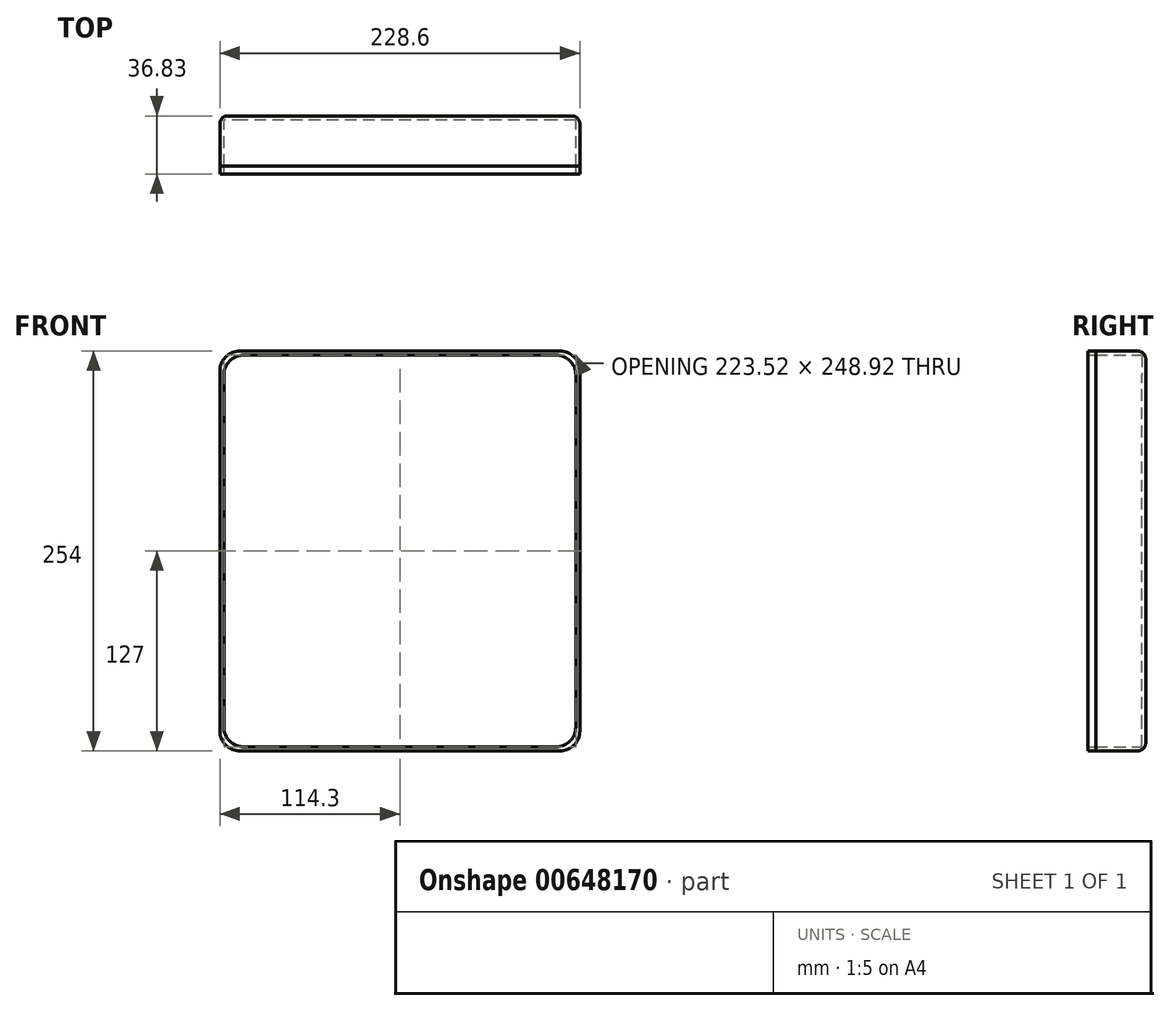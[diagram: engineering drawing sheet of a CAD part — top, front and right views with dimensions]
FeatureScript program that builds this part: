
annotation { "Feature Type Name" : "Feature", "Feature Type Description" : "" }
export const myFeature = defineFeature(function(context is Context, id is Id, definition is map)
    precondition{}
    {
        {
            var Q0;
            Q0=qCreatedBy(makeId("Front.planeOp"),FACE);
            var sketch = newSketch(context, id + "F0", { "sketchPlane" : qUnion([Q0])});
            skLineSegment(sketch, "E0.bottom", {"start": v(101.6, -127) * mm, "end": v(-101.6, -127) * mm});
            skLineSegment(sketch, "E0.top", {"start": v(101.6, 127) * mm, "end": v(-101.6, 127) * mm});
            skLineSegment(sketch, "E0.left", {"start": v(114.3, -114.3) * mm, "end": v(114.3, 114.3) * mm});
            skLineSegment(sketch, "E0.right", {"start": v(-114.3, -114.3) * mm, "end": v(-114.3, 114.3) * mm});
            skPoint(sketch, "E0.middle", {"position": v(0, 0) * mm});
            skPoint(sketch, "E1.visualSharp", {"position": v(-114.3, 127) * mm});
            skArc(sketch, "E1.filletArc", {"start": v(-101.6, 127) * mm, "mid": v(-110.58, 123.28) * mm, "end": v(-114.3, 114.3) * mm});
            skPoint(sketch, "E2.visualSharp", {"position": v(114.3, 127) * mm});
            skArc(sketch, "E2.filletArc", {"start": v(114.3, 114.3) * mm, "mid": v(110.58, 123.28) * mm, "end": v(101.6, 127) * mm});
            skPoint(sketch, "E3.visualSharp", {"position": v(114.3, -127) * mm});
            skArc(sketch, "E3.filletArc", {"start": v(101.6, -127) * mm, "mid": v(110.58, -123.28) * mm, "end": v(114.3, -114.3) * mm});
            skPoint(sketch, "E4.visualSharp", {"position": v(-114.3, -127) * mm});
            skArc(sketch, "E4.filletArc", {"start": v(-114.3, -114.3) * mm, "mid": v(-110.58, -123.28) * mm, "end": v(-101.6, -127) * mm});
            skPoint(sketch, "E5.visualSharp", {"position": v(-110.58, 123.28) * mm});
            skPoint(sketch, "E6.visualSharp", {"position": v(110.58, -123.28) * mm});
            skPoint(sketch, "E7.visualSharp", {"position": v(-110.58, -123.28) * mm});
            skLineSegment(sketch, "E8.bottom", {"start": v(99.06, -124.46) * mm, "end": v(-99.06, -124.46) * mm});
            skLineSegment(sketch, "E8.top", {"start": v(99.06, 124.46) * mm, "end": v(-99.06, 124.46) * mm});
            skLineSegment(sketch, "E8.left", {"start": v(111.76, -111.76) * mm, "end": v(111.76, 111.76) * mm});
            skLineSegment(sketch, "E8.right", {"start": v(-111.76, -111.76) * mm, "end": v(-111.76, 111.76) * mm});
            skPoint(sketch, "E9.visualSharp", {"position": v(111.76, 124.46) * mm});
            skArc(sketch, "E9.filletArc", {"start": v(111.76, 111.76) * mm, "mid": v(108.04, 120.74) * mm, "end": v(99.06, 124.46) * mm});
            skPoint(sketch, "E10.visualSharp", {"position": v(-111.76, 124.46) * mm});
            skArc(sketch, "E10.filletArc", {"start": v(-99.06, 124.46) * mm, "mid": v(-108.04, 120.74) * mm, "end": v(-111.76, 111.76) * mm});
            skPoint(sketch, "E11.visualSharp", {"position": v(-111.76, -124.46) * mm});
            skArc(sketch, "E11.filletArc", {"start": v(-111.76, -111.76) * mm, "mid": v(-108.04, -120.74) * mm, "end": v(-99.06, -124.46) * mm});
            skPoint(sketch, "E12.visualSharp", {"position": v(111.76, -124.46) * mm});
            skArc(sketch, "E12.filletArc", {"start": v(99.06, -124.46) * mm, "mid": v(108.04, -120.74) * mm, "end": v(111.76, -111.76) * mm});
            skSolve(sketch);
        }
        {
            var Q0;
            Q0=qSketchRegion(id+"F0",true);
            extrude(context, id + "F1", {"entities" : qUnion([Q0]), "depth" : 31.75 * mm, "offsetDistance" : 25.4 * mm});
        }
        {
            var Q0;
            Q0=qCreatedBy(makeId("Front.planeOp"),FACE);
            var sketch = newSketch(context, id + "F2", { "sketchPlane" : qUnion([Q0])});
            skLineSegment(sketch, "E13.bottom", {"start": v(-101.6, -127) * mm, "end": v(101.6, -127) * mm});
            skLineSegment(sketch, "E13.top", {"start": v(-101.6, 127) * mm, "end": v(101.6, 127) * mm});
            skLineSegment(sketch, "E13.left", {"start": v(-114.3, -114.3) * mm, "end": v(-114.3, 114.3) * mm});
            skLineSegment(sketch, "E13.right", {"start": v(114.3, -114.3) * mm, "end": v(114.3, 114.3) * mm});
            skPoint(sketch, "E13.middle", {"position": v(0, 0) * mm});
            skPoint(sketch, "E14.visualSharp", {"position": v(-114.3, 127) * mm});
            skArc(sketch, "E14.filletArc", {"start": v(-101.6, 127) * mm, "mid": v(-110.58, 123.28) * mm, "end": v(-114.3, 114.3) * mm});
            skPoint(sketch, "E15.visualSharp", {"position": v(114.3, 127) * mm});
            skArc(sketch, "E15.filletArc", {"start": v(114.3, 114.3) * mm, "mid": v(110.58, 123.28) * mm, "end": v(101.6, 127) * mm});
            skPoint(sketch, "E16.visualSharp", {"position": v(114.3, -127) * mm});
            skArc(sketch, "E16.filletArc", {"start": v(101.6, -127) * mm, "mid": v(110.58, -123.28) * mm, "end": v(114.3, -114.3) * mm});
            skPoint(sketch, "E17.visualSharp", {"position": v(-114.3, -127) * mm});
            skArc(sketch, "E17.filletArc", {"start": v(-114.3, -114.3) * mm, "mid": v(-110.58, -123.28) * mm, "end": v(-101.6, -127) * mm});
            skSolve(sketch);
        }
        {
            var Q0;
            Q0=qSketchRegion(id+"F2",true);
            extrude(context, id + "F3", {"entities" : qUnion([Q0]), "operationType" : NewBodyOperationType.ADD, "depth" : 2.54 * mm, "offsetDistance" : 25.4 * mm});
        }
        {
            var Q0;
            Q0=makeQuery(id+"F1.opExtrude","CAP_FACE",FACE,{"disambiguationData":[OSD([sQuery(id+"F0.wireOp",EDGE,"E0.bottom"),sQuery(id+"F0.wireOp",EDGE,"E0.top"),sQuery(id+"F0.wireOp",EDGE,"E0.left"),sQuery(id+"F0.wireOp",EDGE,"E0.right"),sQuery(id+"F0.wireOp",EDGE,"E1.filletArc"),sQuery(id+"F0.wireOp",EDGE,"E2.filletArc"),sQuery(id+"F0.wireOp",EDGE,"E3.filletArc"),sQuery(id+"F0.wireOp",EDGE,"E4.filletArc"),sQuery(id+"F0.wireOp",EDGE,"s5b6SUju-C0is-XQkz-XXGF-fU9U0Y8NX6aP.bottom"),sQuery(id+"F0.wireOp",EDGE,"s5b6SUju-C0is-XQkz-XXGF-fU9U0Y8NX6aP.top"),sQuery(id+"F0.wireOp",EDGE,"s5b6SUju-C0is-XQkz-XXGF-fU9U0Y8NX6aP.left"),sQuery(id+"F0.wireOp",EDGE,"s5b6SUju-C0is-XQkz-XXGF-fU9U0Y8NX6aP.right"),sQuery(id+"F0.wireOp",EDGE,"E5.filletArc"),sQuery(id+"F0.wireOp",EDGE,"b02a0fa0-6dca-4f1c-a319-37c0052a69da.filletArc"),sQuery(id+"F0.wireOp",EDGE,"E6.filletArc"),sQuery(id+"F0.wireOp",EDGE,"E7.filletArc")])],"isStart":false});
            var sketch = newSketch(context, id + "F4", { "sketchPlane" : qUnion([Q0])});
            skLineSegment(sketch, "E18.bottom", {"start": v(101.6, -127) * mm, "end": v(-101.6, -127) * mm});
            skLineSegment(sketch, "E18.top", {"start": v(101.6, 127) * mm, "end": v(-101.6, 127) * mm});
            skLineSegment(sketch, "E18.left", {"start": v(114.3, -114.3) * mm, "end": v(114.3, 114.3) * mm});
            skLineSegment(sketch, "E18.right", {"start": v(-114.3, -114.3) * mm, "end": v(-114.3, 114.3) * mm});
            skPoint(sketch, "E18.middle", {"position": v(0, 0) * mm});
            skPoint(sketch, "E19.visualSharp", {"position": v(-114.3, 127) * mm});
            skArc(sketch, "E19.filletArc", {"start": v(-101.6, 127) * mm, "mid": v(-110.58, 123.28) * mm, "end": v(-114.3, 114.3) * mm});
            skPoint(sketch, "E20.visualSharp", {"position": v(114.3, 127) * mm});
            skArc(sketch, "E20.filletArc", {"start": v(114.3, 114.3) * mm, "mid": v(110.58, 123.28) * mm, "end": v(101.6, 127) * mm});
            skPoint(sketch, "E21.visualSharp", {"position": v(114.3, -127) * mm});
            skArc(sketch, "E21.filletArc", {"start": v(101.6, -127) * mm, "mid": v(110.58, -123.28) * mm, "end": v(114.3, -114.3) * mm});
            skPoint(sketch, "E22.visualSharp", {"position": v(-114.3, -127) * mm});
            skArc(sketch, "E22.filletArc", {"start": v(-114.3, -114.3) * mm, "mid": v(-110.58, -123.28) * mm, "end": v(-101.6, -127) * mm});
            skPoint(sketch, "E23.visualSharp", {"position": v(-110.58, 123.28) * mm});
            skPoint(sketch, "E24.visualSharp", {"position": v(110.58, -123.28) * mm});
            skPoint(sketch, "E25.visualSharp", {"position": v(-106.9, -119.17) * mm});
            skLineSegment(sketch, "E26.bottom", {"start": v(99.06, -124.46) * mm, "end": v(-99.06, -124.46) * mm});
            skLineSegment(sketch, "E26.top", {"start": v(99.06, 124.46) * mm, "end": v(-99.06, 124.46) * mm});
            skLineSegment(sketch, "E26.left", {"start": v(111.76, -111.76) * mm, "end": v(111.76, 111.76) * mm});
            skLineSegment(sketch, "E26.right", {"start": v(-111.76, -111.76) * mm, "end": v(-111.76, 111.76) * mm});
            skPoint(sketch, "E27.visualSharp", {"position": v(111.76, 124.46) * mm});
            skArc(sketch, "E27.filletArc", {"start": v(111.76, 111.76) * mm, "mid": v(108.04, 120.74) * mm, "end": v(99.06, 124.46) * mm});
            skPoint(sketch, "E28.visualSharp", {"position": v(-111.76, 124.46) * mm});
            skArc(sketch, "E28.filletArc", {"start": v(-99.06, 124.46) * mm, "mid": v(-108.04, 120.74) * mm, "end": v(-111.76, 111.76) * mm});
            skPoint(sketch, "E29.visualSharp", {"position": v(-111.76, -124.46) * mm});
            skArc(sketch, "E29.filletArc", {"start": v(-111.76, -111.76) * mm, "mid": v(-108.04, -120.74) * mm, "end": v(-99.06, -124.46) * mm});
            skPoint(sketch, "E30.visualSharp", {"position": v(111.76, -124.46) * mm});
            skArc(sketch, "E30.filletArc", {"start": v(99.06, -124.46) * mm, "mid": v(108.04, -120.74) * mm, "end": v(111.76, -111.76) * mm});
            skSolve(sketch);
        }
        {
            var Q0;
            Q0=qSketchRegion(id+"F4",true);
            extrude(context, id + "F5", {"entities" : qUnion([Q0]), "depth" : 5.08 * mm, "offsetDistance" : 25.4 * mm});
        }
        {
            var Q0;
            Q0=makeQuery(id+"F3.boolean.opBoolean","MERGE",FACE,{"derivedFrom":[makeQuery(id+"F1.opExtrude","CAP_FACE",FACE,{"disambiguationData":[OSD([sQuery(id+"F0.wireOp",EDGE,"E0.bottom"),sQuery(id+"F0.wireOp",EDGE,"E0.top"),sQuery(id+"F0.wireOp",EDGE,"E0.left"),sQuery(id+"F0.wireOp",EDGE,"E0.right"),sQuery(id+"F0.wireOp",EDGE,"E1.filletArc"),sQuery(id+"F0.wireOp",EDGE,"E2.filletArc"),sQuery(id+"F0.wireOp",EDGE,"E3.filletArc"),sQuery(id+"F0.wireOp",EDGE,"E4.filletArc"),sQuery(id+"F0.wireOp",EDGE,"E8.bottom"),sQuery(id+"F0.wireOp",EDGE,"E8.top"),sQuery(id+"F0.wireOp",EDGE,"E8.left"),sQuery(id+"F0.wireOp",EDGE,"E8.right"),sQuery(id+"F0.wireOp",EDGE,"E9.filletArc"),sQuery(id+"F0.wireOp",EDGE,"E10.filletArc"),sQuery(id+"F0.wireOp",EDGE,"E11.filletArc"),sQuery(id+"F0.wireOp",EDGE,"E12.filletArc")])],"isStart":true}),makeQuery(id+"F3.opExtrude","CAP_FACE",FACE,{"disambiguationData":[OSD([sQuery(id+"F2.wireOp",EDGE,"E13.bottom"),sQuery(id+"F2.wireOp",EDGE,"E13.top"),sQuery(id+"F2.wireOp",EDGE,"E13.left"),sQuery(id+"F2.wireOp",EDGE,"E13.right"),sQuery(id+"F2.wireOp",EDGE,"E14.filletArc"),sQuery(id+"F2.wireOp",EDGE,"E15.filletArc"),sQuery(id+"F2.wireOp",EDGE,"E16.filletArc"),sQuery(id+"F2.wireOp",EDGE,"E17.filletArc")])],"isStart":true})]});
            fillet(context, id + "F6", {"entities" : qUnion([Q0]), "radius" : 5.08 * mm, "tangentPropagation" : true, "allowEdgeOverflow" : false});
        }
    });
